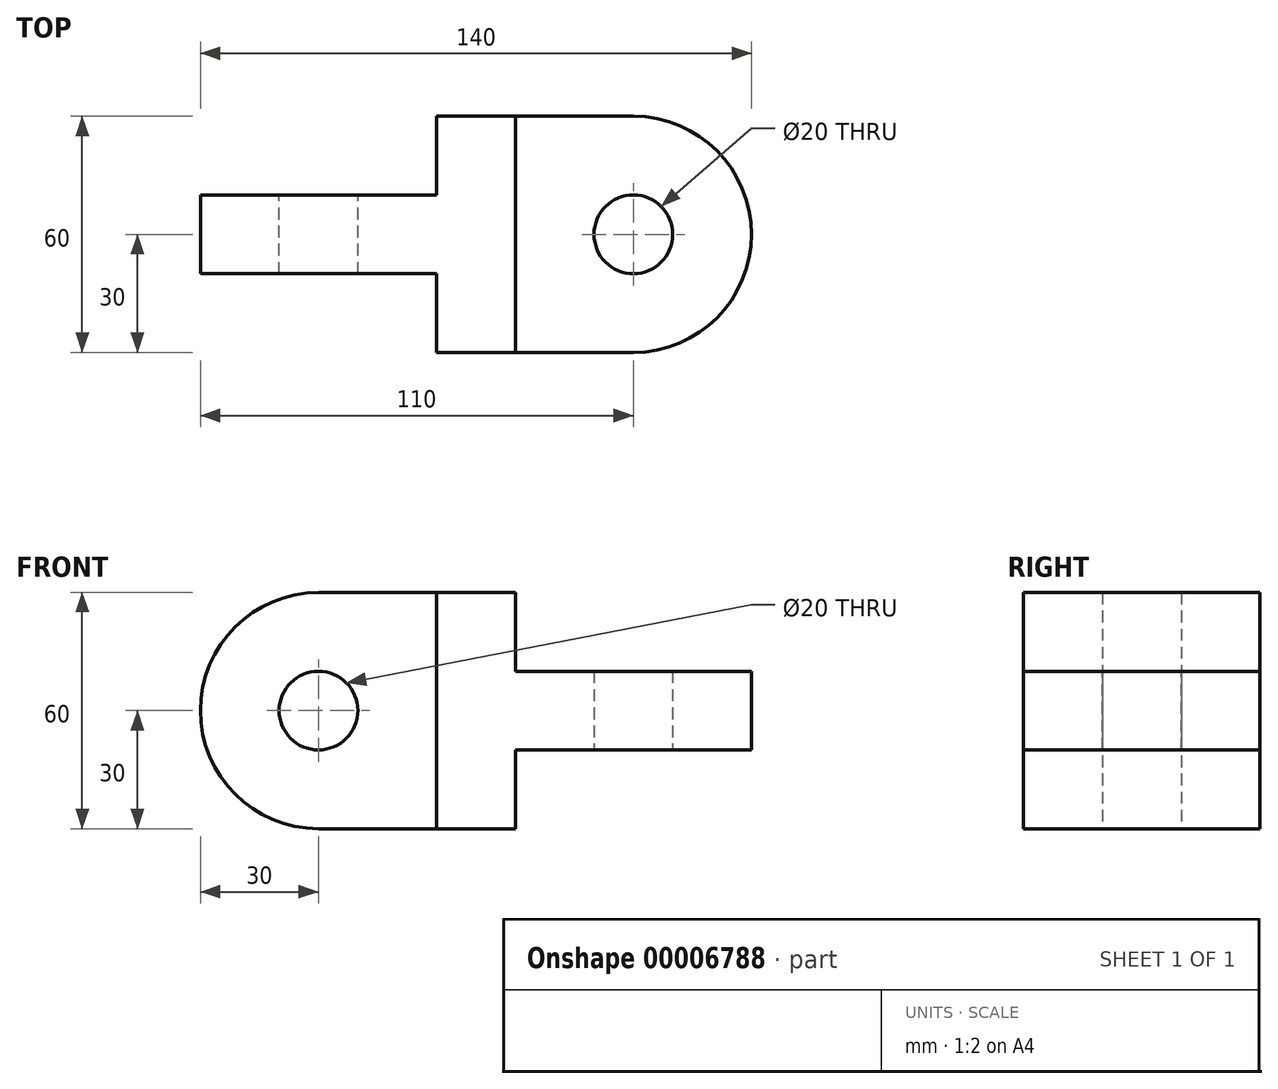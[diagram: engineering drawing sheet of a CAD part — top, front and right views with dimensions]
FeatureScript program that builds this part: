
annotation { "Feature Type Name" : "Feature", "Feature Type Description" : "" }
export const myFeature = defineFeature(function(context is Context, id is Id, definition is map)
    precondition{}
    {
        {
            var Q0;
            Q0=qCreatedBy(makeId("Right.planeOp"),FACE);
            var sketch = newSketch(context, id + "F0", { "sketchPlane" : qUnion([Q0])});
            skLineSegment(sketch, "E0.rect.bottom", {"start": v(-30, -30) * mm, "end": v(30, -30) * mm});
            skLineSegment(sketch, "E0.rect.top", {"start": v(-30, 30) * mm, "end": v(30, 30) * mm});
            skLineSegment(sketch, "E0.rect.left", {"start": v(-30, -30) * mm, "end": v(-30, 30) * mm});
            skLineSegment(sketch, "E0.rect.right", {"start": v(30, -30) * mm, "end": v(30, 30) * mm});
            skPoint(sketch, "E0.rect.middle", {"position": v(0, 0) * mm});
            skSolve(sketch);
        }
        {
            var Q0;
            Q0 = qSketchRegion(id + "F0", true);
            extrude(context, id + "F1", {"entities" : qUnion([Q0]), "depth" : 20 * mm, "symmetric" : true});
        }
        {
            var Q0;
            Q0=qCreatedBy(makeId("Top.planeOp"),FACE);
            var sketch = newSketch(context, id + "F2", { "sketchPlane" : qUnion([Q0])});
            skLineSegment(sketch, "E1", {"start": v(10, 30) * mm, "end": v(40, 30) * mm});
            skArc(sketch, "E2", {"start": v(40, 30) * mm, "mid": v(70, 0) * mm, "end": v(40, -30) * mm});
            skLineSegment(sketch, "E3", {"start": v(40, -30) * mm, "end": v(10, -30) * mm});
            skLineSegment(sketch, "E4", {"start": v(10, -30) * mm, "end": v(10, 30) * mm});
            skCircle(sketch, "E5", {"center": v(40, 0) * mm, "radius": 10 * mm});
            skSolve(sketch);
        }
        {
            var Q0;
            Q0 = qSketchRegion(id + "F2", true);
            extrude(context, id + "F3", {"entities" : qUnion([Q0]), "operationType" : NewBodyOperationType.ADD, "depth" : 20 * mm, "symmetric" : true});
        }
        {
            var Q0;
            Q0=qCreatedBy(makeId("Front.planeOp"),FACE);
            var sketch = newSketch(context, id + "F4", { "sketchPlane" : qUnion([Q0])});
            skLineSegment(sketch, "E6", {"start": v(-10, 30) * mm, "end": v(-10, -30) * mm});
            skLineSegment(sketch, "E7", {"start": v(-10, -30) * mm, "end": v(-40, -30) * mm});
            skArc(sketch, "E8", {"start": v(-40, -30) * mm, "mid": v(-70, 0) * mm, "end": v(-40, 30) * mm});
            skLineSegment(sketch, "E9", {"start": v(-40, 30) * mm, "end": v(-10, 30) * mm});
            skCircle(sketch, "E10", {"center": v(-40, 0) * mm, "radius": 10 * mm});
            skSolve(sketch);
        }
        {
            var Q0;
            Q0 = qSketchRegion(id + "F4", true);
            extrude(context, id + "F5", {"entities" : qUnion([Q0]), "operationType" : NewBodyOperationType.ADD, "depth" : 20 * mm, "symmetric" : true});
        }
    });
